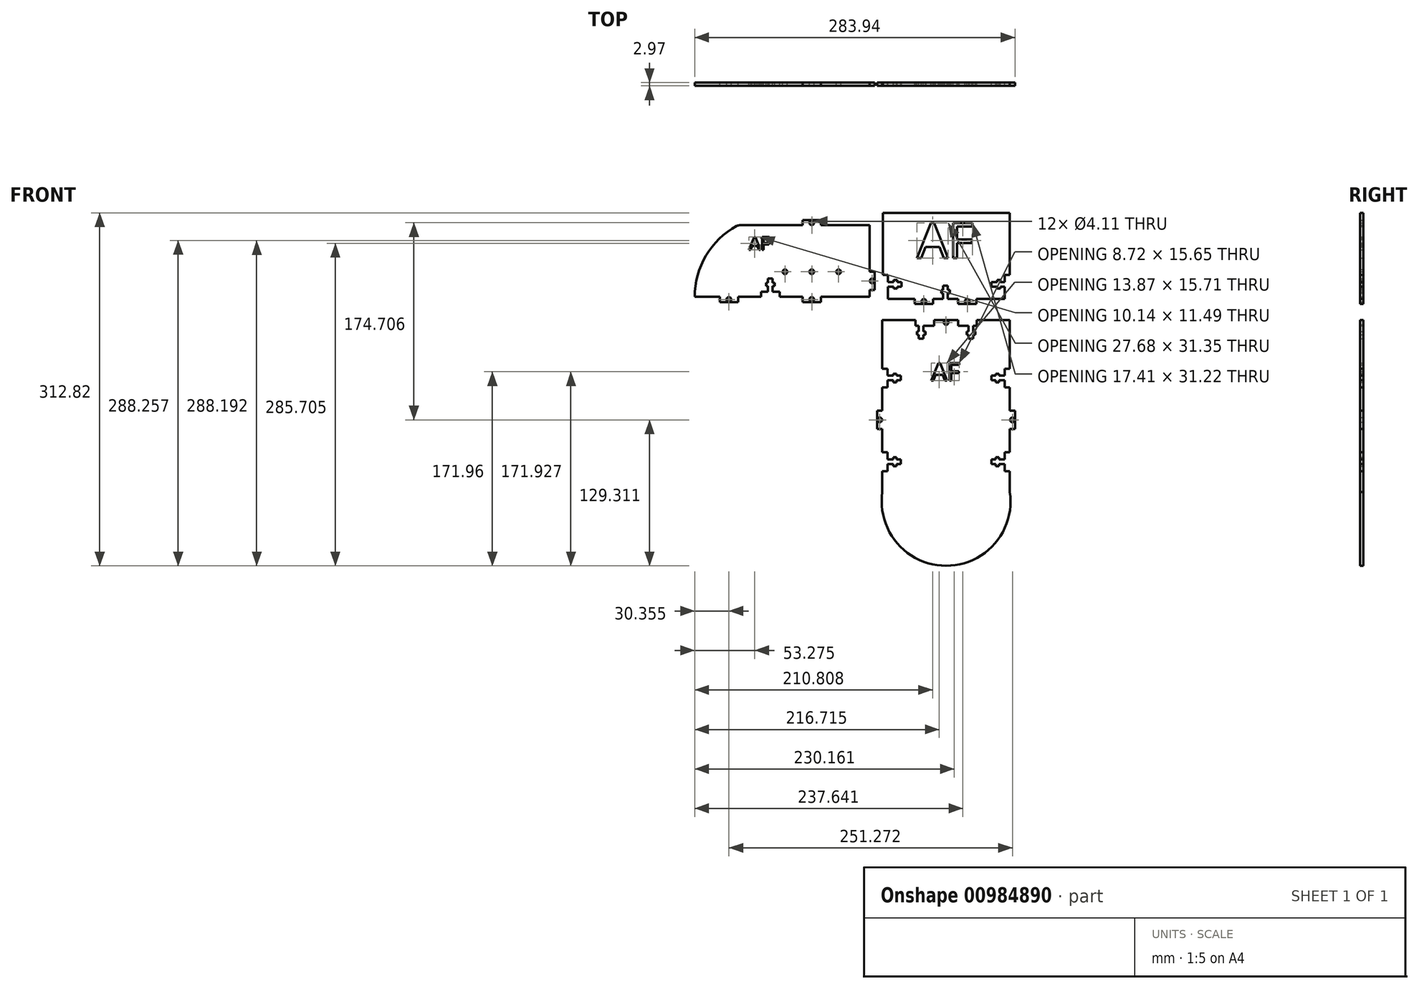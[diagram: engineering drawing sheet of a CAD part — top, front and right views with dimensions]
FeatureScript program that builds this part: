
annotation { "Feature Type Name" : "Feature", "Feature Type Description" : "" }
export const myFeature = defineFeature(function(context is Context, id is Id, definition is map)
    precondition{}
    {
        {
            var Q0;
            Q0=qCreatedBy(makeId("Front.planeOp"),FACE);
            var sketch = newSketch(context, id + "F0", { "sketchPlane" : qUnion([Q0])});
            skCircle(sketch, "E0", {"center": v(-10.51, -12.98) * mm, "radius": 2.06 * mm});
            skLineSegment(sketch, "E1.top", {"start": v(-18.6, -15.29) * mm, "end": v(-2.43, -15.29) * mm});
            skCircle(sketch, "E2", {"center": v(27.94, -12.98) * mm, "radius": 2.06 * mm});
            skLineSegment(sketch, "E3", {"start": v(19.85, -15.29) * mm, "end": v(36.02, -15.29) * mm});
            skLineSegment(sketch, "E4", {"start": v(-38.26, -10.74) * mm, "end": v(-18.6, -10.74) * mm});
            skLineSegment(sketch, "E5", {"start": v(-2.43, -15.29) * mm, "end": v(-2.43, -10.74) * mm});
            skLineSegment(sketch, "E6", {"start": v(-18.6, -15.29) * mm, "end": v(-18.6, -10.74) * mm});
            skLineSegment(sketch, "E7", {"start": v(36.02, -15.29) * mm, "end": v(36.02, -10.74) * mm});
            skLineSegment(sketch, "E8", {"start": v(19.85, -15.29) * mm, "end": v(19.85, -10.74) * mm});
            skLineSegment(sketch, "E9.trimOffspring", {"start": v(-2.43, -10.74) * mm, "end": v(6.65, -10.74) * mm});
            skLineSegment(sketch, "E10.trimOffspring", {"start": v(36.02, -10.74) * mm, "end": v(58.06, -10.74) * mm});
            skLineSegment(sketch, "E11", {"start": v(-38.26, -10.74) * mm, "end": v(-42.22, -10.74) * mm});
            skLineSegment(sketch, "E12", {"start": v(58.06, -10.74) * mm, "end": v(61.06, -10.74) * mm});
            skLineSegment(sketch, "E13", {"start": v(65.6, 14.43) * mm, "end": v(65.6, 10.39) * mm});
            skLineSegment(sketch, "E14", {"start": v(-46.77, 14.3) * mm, "end": v(-46.77, 10.39) * mm});
            skLineSegment(sketch, "E15", {"start": v(-46.77, 10.39) * mm, "end": v(-42.22, 10.39) * mm});
            skLineSegment(sketch, "E16", {"start": v(-42.22, 10.39) * mm, "end": v(-42.22, 4.11) * mm});
            skLineSegment(sketch, "E17", {"start": v(65.6, 10.39) * mm, "end": v(61.06, 10.39) * mm});
            skLineSegment(sketch, "E18", {"start": v(61.06, 10.39) * mm, "end": v(61.06, 4.11) * mm});
            skLineSegment(sketch, "E19", {"start": v(61.06, 0) * mm, "end": v(57.32, 0) * mm});
            skLineSegment(sketch, "E20.trimOffspring", {"start": v(61.06, 0) * mm, "end": v(61.06, -6.27) * mm});
            skLineSegment(sketch, "E21", {"start": v(-42.22, 0) * mm, "end": v(-37.14, 0) * mm});
            skLineSegment(sketch, "E22.trimOffspring", {"start": v(-42.22, 0) * mm, "end": v(-42.22, -6.27) * mm});
            skLineSegment(sketch, "E23", {"start": v(6.65, -10.74) * mm, "end": v(6.65, -5.66) * mm});
            skLineSegment(sketch, "E24.trimOffspring", {"start": v(10.77, -10.74) * mm, "end": v(19.85, -10.74) * mm});
            skLineSegment(sketch, "E25", {"start": v(-46.77, 14.3) * mm, "end": v(-46.77, 65.46) * mm});
            skLineSegment(sketch, "E26", {"start": v(65.6, 14.43) * mm, "end": v(65.6, 65.46) * mm});
            skLineSegment(sketch, "E27", {"start": v(-46.77, 65.46) * mm, "end": v(65.6, 65.46) * mm});
            skLineSegment(sketch, "E28.trimOffspring", {"start": v(-30.47, 4.11) * mm, "end": v(-34.21, 4.11) * mm});
            skLineSegment(sketch, "E29.trimOffspring", {"start": v(49.32, 4.11) * mm, "end": v(54.4, 4.11) * mm});
            skLineSegment(sketch, "E30.trimOffspring", {"start": v(10.77, 1) * mm, "end": v(10.77, -2.74) * mm});
            skLineSegment(sketch, "E31", {"start": v(49.32, 4.11) * mm, "end": v(49.32, 0) * mm});
            skPoint(sketch, "E32.startSnap0", {"position": v(49.32, -3.14) * mm});
            skPoint(sketch, "E33.end.orphan", {"position": v(49.32, 10.39) * mm});
            skPoint(sketch, "E34.end.orphan", {"position": v(43.4, 10.39) * mm});
            skPoint(sketch, "E35.end.orphan", {"position": v(43.4, 4.11) * mm});
            skPoint(sketch, "E36.end.orphan", {"position": v(37.56, 4.11) * mm});
            skPoint(sketch, "E37.trimOffspring.end.orphan", {"position": v(37.56, 0) * mm});
            skPoint(sketch, "E38.end.orphan", {"position": v(43.4, 0) * mm});
            skPoint(sketch, "E39.end.orphan", {"position": v(43.4, -6.27) * mm});
            skPoint(sketch, "E40.orphan", {"position": v(49.32, -6.27) * mm});
            skLineSegment(sketch, "E41", {"start": v(54.4, -1.78) * mm, "end": v(57.32, -1.78) * mm});
            skLineSegment(sketch, "E42", {"start": v(57.32, -1.78) * mm, "end": v(57.32, 0) * mm});
            skLineSegment(sketch, "E43", {"start": v(54.4, 4.11) * mm, "end": v(54.4, 5.9) * mm});
            skLineSegment(sketch, "E44", {"start": v(54.4, 5.9) * mm, "end": v(57.3, 5.9) * mm});
            skLineSegment(sketch, "E45", {"start": v(57.3, 5.9) * mm, "end": v(57.3, 4.11) * mm});
            skLineSegment(sketch, "E46.trimOffspring", {"start": v(57.3, 4.11) * mm, "end": v(61.06, 4.11) * mm});
            skLineSegment(sketch, "E47", {"start": v(54.4, 0) * mm, "end": v(54.4, -1.78) * mm});
            skLineSegment(sketch, "E48.trimOffspring", {"start": v(54.4, 0) * mm, "end": v(49.32, 0) * mm});
            skLineSegment(sketch, "E49", {"start": v(-30.47, 4.11) * mm, "end": v(-30.47, 0) * mm});
            skLineSegment(sketch, "E50", {"start": v(6.65, 1) * mm, "end": v(10.77, 1) * mm});
            skLineSegment(sketch, "E51", {"start": v(61.06, -6.27) * mm, "end": v(61.06, -10.74) * mm});
            skPoint(sketch, "E52.orphan", {"position": v(65.6, -10.74) * mm});
            skPoint(sketch, "E53.start.orphan", {"position": v(65.6, -6.27) * mm});
            skLineSegment(sketch, "E54", {"start": v(-42.22, -6.27) * mm, "end": v(-42.22, -10.74) * mm});
            skPoint(sketch, "E55.orphan", {"position": v(-46.77, -10.74) * mm});
            skLineSegment(sketch, "E56", {"start": v(-37.14, 4.11) * mm, "end": v(-37.14, 5.9) * mm});
            skLineSegment(sketch, "E57", {"start": v(-37.14, 5.9) * mm, "end": v(-34.21, 5.9) * mm});
            skLineSegment(sketch, "E58", {"start": v(-34.21, 5.9) * mm, "end": v(-34.21, 4.11) * mm});
            skLineSegment(sketch, "E59.trimOffspring", {"start": v(-37.14, 4.11) * mm, "end": v(-42.22, 4.11) * mm});
            skLineSegment(sketch, "E60.trimOffspring", {"start": v(-34.21, 0) * mm, "end": v(-30.47, 0) * mm});
            skLineSegment(sketch, "E61", {"start": v(-37.14, 0) * mm, "end": v(-37.14, -1.75) * mm});
            skLineSegment(sketch, "E62", {"start": v(-37.14, -1.75) * mm, "end": v(-34.21, -1.75) * mm});
            skLineSegment(sketch, "E63", {"start": v(-34.21, -1.75) * mm, "end": v(-34.21, 0) * mm});
            skLineSegment(sketch, "E64", {"start": v(4.88, -5.66) * mm, "end": v(6.65, -5.66) * mm});
            skLineSegment(sketch, "E65", {"start": v(4.88, -5.66) * mm, "end": v(4.88, -2.74) * mm});
            skLineSegment(sketch, "E66", {"start": v(4.88, -2.74) * mm, "end": v(6.65, -2.74) * mm});
            skLineSegment(sketch, "E67", {"start": v(10.77, -5.66) * mm, "end": v(12.55, -5.66) * mm});
            skLineSegment(sketch, "E68", {"start": v(12.55, -5.66) * mm, "end": v(12.55, -2.74) * mm});
            skLineSegment(sketch, "E69", {"start": v(12.55, -2.74) * mm, "end": v(10.77, -2.74) * mm});
            skLineSegment(sketch, "E70.trimOffspring", {"start": v(10.77, -5.66) * mm, "end": v(10.77, -10.74) * mm});
            skLineSegment(sketch, "E71.trimOffspring", {"start": v(6.65, -2.74) * mm, "end": v(6.65, 1) * mm});
            skText(sketch, "E72", { "text": "AF", "fontName": "OpenSans-Regular.ttf"});
            const initialGuessF0  = {"E72": [-0.0167, 0.02522, 1, 0, 0.03149]};
            skSetInitialGuess(sketch, initialGuessF0);
            skSolve(sketch);
        }
        {
            var Q0;
            Q0=makeQuery(id+"F0.imprint","IMPRINT",FACE,{"disambiguationData":[TD([[makeQuery(id+"F0.imprint","IMPRINT",EDGE,{"derivedFrom":sQuery(id+"F0.wireOp",EDGE,"E0")}),-1.0]])]});
            extrude(context, id + "F1", {"entities" : qUnion([Q0]), "depth" : 2.97 * mm, "offsetDistance" : 25.4 * mm});
        }
        {
            var Q0;
            Q0=qCreatedBy(makeId("Front.planeOp"),FACE);
            var sketch = newSketch(context, id + "F2", { "sketchPlane" : qUnion([Q0])});
            skLineSegment(sketch, "E73", {"start": v(-36, -9.08) * mm, "end": v(-36, -2.95) * mm});
            skLineSegment(sketch, "E74", {"start": v(-31.45, -2.95) * mm, "end": v(-31.45, 13.2) * mm});
            skLineSegment(sketch, "E75", {"start": v(-31.45, 13.2) * mm, "end": v(-36, 13.2) * mm});
            skLineSegment(sketch, "E76", {"start": v(-31.45, -2.95) * mm, "end": v(-36, -2.95) * mm});
            skCircle(sketch, "E77", {"center": v(-33.76, 5.12) * mm, "radius": 2.06 * mm});
            skLineSegment(sketch, "E78", {"start": v(-36, -9.08) * mm, "end": v(-79.18, -9.08) * mm});
            skLineSegment(sketch, "E79", {"start": v(-79.18, -13.62) * mm, "end": v(-79.18, -9.08) * mm});
            skLineSegment(sketch, "E80", {"start": v(-79.18, -13.62) * mm, "end": v(-95.33, -13.62) * mm});
            skLineSegment(sketch, "E81", {"start": v(-95.33, -13.62) * mm, "end": v(-95.33, -9.08) * mm});
            skCircle(sketch, "E82", {"center": v(-87.25, -11.31) * mm, "radius": 2.06 * mm});
            skPoint(sketch, "E82.centerSnap0", {"position": v(-87.25, -13.62) * mm});
            skLineSegment(sketch, "E83", {"start": v(-115.65, -9.08) * mm, "end": v(-115.65, -4.53) * mm});
            skLineSegment(sketch, "E84", {"start": v(-132.31, -9.08) * mm, "end": v(-132.31, -4.53) * mm});
            skLineSegment(sketch, "E85", {"start": v(-132.31, -4.53) * mm, "end": v(-126.04, -4.53) * mm});
            skLineSegment(sketch, "E86.trimOffspring", {"start": v(-132.31, -9.08) * mm, "end": v(-152.63, -9.08) * mm});
            skLineSegment(sketch, "E87", {"start": v(-126.04, -4.53) * mm, "end": v(-126.04, 0.55) * mm});
            skLineSegment(sketch, "E88", {"start": v(-152.63, -13.62) * mm, "end": v(-152.63, -9.08) * mm});
            skLineSegment(sketch, "E89", {"start": v(-152.63, -13.62) * mm, "end": v(-168.79, -13.62) * mm});
            skLineSegment(sketch, "E90", {"start": v(-168.79, -13.62) * mm, "end": v(-168.79, -9.08) * mm});
            skCircle(sketch, "E91", {"center": v(-160.7, -11.31) * mm, "radius": 2.06 * mm});
            skPoint(sketch, "E91.centerSnap0", {"position": v(-160.7, -13.62) * mm});
            skLineSegment(sketch, "E92", {"start": v(-36, 54.42) * mm, "end": v(-79.18, 54.42) * mm});
            skPoint(sketch, "E93.centerSnap0", {"position": v(-124.36, 18.96) * mm});
            skLineSegment(sketch, "E94.trimOffspring", {"start": v(-95.33, -9.08) * mm, "end": v(-115.65, -9.08) * mm});
            skLineSegment(sketch, "E95.trimOffspring", {"start": v(-36, 13.2) * mm, "end": v(-36, 54.42) * mm});
            skLineSegment(sketch, "E96", {"start": v(-191.06, -9.08) * mm, "end": v(-168.79, -9.08) * mm});
            skPoint(sketch, "E97.start.orphan", {"position": v(-126.81, 13.13) * mm});
            skLineSegment(sketch, "E98", {"start": v(-126.04, 7.22) * mm, "end": v(-121.92, 7.22) * mm});
            skLineSegment(sketch, "E99", {"start": v(-121.92, -4.53) * mm, "end": v(-115.65, -4.53) * mm});
            skLineSegment(sketch, "E100", {"start": v(-121.92, 7.22) * mm, "end": v(-121.92, 3.47) * mm});
            skLineSegment(sketch, "E101", {"start": v(-121.92, 0.55) * mm, "end": v(-120.15, 0.55) * mm});
            skPoint(sketch, "E101.startSnap0", {"position": v(-121.92, 1.34) * mm});
            skLineSegment(sketch, "E102", {"start": v(-120.15, 0.55) * mm, "end": v(-120.15, 3.47) * mm});
            skLineSegment(sketch, "E103", {"start": v(-120.15, 3.47) * mm, "end": v(-121.92, 3.47) * mm});
            skLineSegment(sketch, "E104", {"start": v(-126.04, 3.47) * mm, "end": v(-127.82, 3.47) * mm});
            skLineSegment(sketch, "E105", {"start": v(-127.82, 3.47) * mm, "end": v(-127.82, 0.55) * mm});
            skLineSegment(sketch, "E106", {"start": v(-127.82, 0.55) * mm, "end": v(-126.04, 0.55) * mm});
            skLineSegment(sketch, "E107.trimOffspring", {"start": v(-126.04, 3.47) * mm, "end": v(-126.04, 7.22) * mm});
            skLineSegment(sketch, "E108.trimOffspring", {"start": v(-121.92, 0.55) * mm, "end": v(-121.92, -4.53) * mm});
            skLineSegment(sketch, "E109.trimOffspring", {"start": v(-168.79, 54.42) * mm, "end": v(-191.06, 54.42) * mm});
            skPoint(sketch, "E110", {"position": v(-87.25, 13.2) * mm});
            skCircle(sketch, "E111", {"center": v(-87.25, 13.2) * mm, "radius": 2.06 * mm});
            skCircle(sketch, "E112", {"center": v(-110.98, 13.2) * mm, "radius": 2.06 * mm});
            skCircle(sketch, "E113", {"center": v(-63.53, 13.2) * mm, "radius": 2.06 * mm});
            skLineSegment(sketch, "E114", {"start": v(-191.06, 54.42) * mm, "end": v(-191.06, -9.08) * mm});
            skLineSegment(sketch, "E115", {"start": v(-168.79, 54.42) * mm, "end": v(-152.63, 54.42) * mm});
            skLineSegment(sketch, "E116", {"start": v(-95.33, 54.42) * mm, "end": v(-95.33, 58.97) * mm});
            skLineSegment(sketch, "E117", {"start": v(-95.33, 58.97) * mm, "end": v(-79.18, 58.97) * mm});
            skLineSegment(sketch, "E118", {"start": v(-79.18, 58.97) * mm, "end": v(-79.18, 54.42) * mm});
            skCircle(sketch, "E119", {"center": v(-87.25, 56.66) * mm, "radius": 2.06 * mm});
            skPoint(sketch, "E119.centerSnap0", {"position": v(-87.25, 58.97) * mm});
            skLineSegment(sketch, "E120.trimOffspring", {"start": v(-95.33, 54.42) * mm, "end": v(-152.63, 54.42) * mm});
            skArc(sketch, "E121", {"start": v(-152.63, 54.42) * mm, "mid": v(-180.7, 28.03) * mm, "end": v(-191.06, -9.08) * mm});
            skText(sketch, "E122", { "text": "AF", "fontName": "OpenSans-Regular.ttf"});
            const initialGuessF2  = {"E122": [-0.14286, 0.0326, 1, 0, 0.01154]};
            skSetInitialGuess(sketch, initialGuessF2);
            skSolve(sketch);
        }
        {
            var Q0;
            {var subQ1=sQuery(id+"F2.wireOp",EDGE,"OVJFDN25-UqmM-4DHd-mgfS-xPrGIr8piSGO");Q0=makeQuery(id+"F2.imprint","IMPRINT",FACE,{"disambiguationData":[TD([[makeQuery(id+"F2.imprint","IMPRINT",EDGE,{"derivedFrom":subQ1}),-1.0]])]});}
            var Q1;
            {var subQ2=sQuery(id+"F2.wireOp",EDGE,"OVJFDN25-UqmM-4DHd-mgfS-xPrGIr8piSGO");Q1=makeQuery(id+"F2.imprint","IMPRINT",FACE,{"disambiguationData":[TD([[makeQuery(id+"F2.imprint","IMPRINT",EDGE,{"derivedFrom":subQ2}),1.0]])]});}
            var Q2;
            {var subQ1=sQuery(id+"F2.wireOp",EDGE,"E79");Q2=makeQuery(id+"F2.imprint","IMPRINT",FACE,{"disambiguationData":[TD([[makeQuery(id+"F2.imprint","IMPRINT",EDGE,{"derivedFrom":subQ1}),1.0]])]});}
            extrude(context, id + "F3", {"entities" : qUnion([Q0, Q1, Q2]), "depth" : 2.97 * mm, "offsetDistance" : 25.4 * mm});
        }
        {
            var Q0;
            Q0=qCreatedBy(makeId("Front.planeOp"),FACE);
            var sketch = newSketch(context, id + "F4", { "sketchPlane" : qUnion([Q0])});
            skLineSegment(sketch, "E123", {"start": v(-47.3, -38.57) * mm, "end": v(-17.97, -38.57) * mm});
            skLineSegment(sketch, "E124", {"start": v(65.7, -38.57) * mm, "end": v(65.7, -81.75) * mm});
            skLineSegment(sketch, "E125", {"start": v(-47.3, -38.57) * mm, "end": v(-47.3, -81.75) * mm});
            skLineSegment(sketch, "E126", {"start": v(-47.3, -190.97) * mm, "end": v(65.7, -190.97) * mm});
            skLineSegment(sketch, "E127", {"start": v(65.7, -38.57) * mm, "end": v(35.47, -38.57) * mm});
            skLineSegment(sketch, "E128", {"start": v(-1.3, -43.64) * mm, "end": v(-1.3, -38.57) * mm});
            skLineSegment(sketch, "E129", {"start": v(-1.3, -43.64) * mm, "end": v(-10.82, -43.64) * mm});
            skLineSegment(sketch, "E130.trimOffspring", {"start": v(-1.3, -38.57) * mm, "end": v(19.7, -38.57) * mm});
            skLineSegment(sketch, "E131.trimOffspring", {"start": v(35.47, -38.57) * mm, "end": v(65.7, -38.57) * mm});
            skCircle(sketch, "E132", {"center": v(9.2, -40.88) * mm, "radius": 2.06 * mm});
            skLineSegment(sketch, "E133", {"start": v(-17.97, -43.64) * mm, "end": v(-17.97, -38.57) * mm});
            skLineSegment(sketch, "E134", {"start": v(35.47, -38.57) * mm, "end": v(36.36, -38.57) * mm});
            skLineSegment(sketch, "E135", {"start": v(-17.97, -43.64) * mm, "end": v(-14.94, -43.64) * mm});
            skLineSegment(sketch, "E136", {"start": v(-14.94, -43.64) * mm, "end": v(-14.94, -48.72) * mm});
            skPoint(sketch, "E137.end.orphan", {"position": v(-8.78, -55.39) * mm});
            skLineSegment(sketch, "E138", {"start": v(-10.82, -43.64) * mm, "end": v(-10.82, -48.72) * mm});
            skLineSegment(sketch, "E139", {"start": v(-47.3, -81.75) * mm, "end": v(-42.74, -81.75) * mm});
            skLineSegment(sketch, "E140", {"start": v(-42.74, -98.41) * mm, "end": v(-47.3, -98.41) * mm});
            skLineSegment(sketch, "E141.trimOffspring", {"start": v(-47.3, -98.41) * mm, "end": v(-47.3, -119.12) * mm});
            skLineSegment(sketch, "E142", {"start": v(-42.74, -81.75) * mm, "end": v(-42.74, -88.02) * mm});
            skLineSegment(sketch, "E143", {"start": v(-42.74, -98.41) * mm, "end": v(-42.74, -92.14) * mm});
            skPoint(sketch, "E144.start.orphan", {"position": v(-42.74, -38.57) * mm});
            skLineSegment(sketch, "E145", {"start": v(-47.3, -119.12) * mm, "end": v(-51.88, -119.12) * mm});
            skLineSegment(sketch, "E146", {"start": v(-51.88, -119.12) * mm, "end": v(-51.88, -135.27) * mm});
            skLineSegment(sketch, "E147", {"start": v(-51.88, -135.27) * mm, "end": v(-47.3, -135.27) * mm});
            skPoint(sketch, "E148.start.orphan", {"position": v(-42.74, -118.73) * mm});
            skLineSegment(sketch, "E149.trimOffspring", {"start": v(-47.3, -135.27) * mm, "end": v(-47.3, -155.97) * mm});
            skCircle(sketch, "E150", {"center": v(-49.57, -127.2) * mm, "radius": 2.06 * mm});
            skLineSegment(sketch, "E151", {"start": v(-47.3, -155.97) * mm, "end": v(-42.74, -155.97) * mm});
            skLineSegment(sketch, "E152", {"start": v(-42.74, -172.63) * mm, "end": v(-47.3, -172.63) * mm});
            skLineSegment(sketch, "E153.trimOffspring", {"start": v(-47.3, -172.63) * mm, "end": v(-47.3, -190.97) * mm});
            skLineSegment(sketch, "E154", {"start": v(-42.74, -172.63) * mm, "end": v(-42.74, -166.36) * mm});
            skLineSegment(sketch, "E155", {"start": v(-42.74, -155.97) * mm, "end": v(-42.74, -162.24) * mm});
            skLineSegment(sketch, "E156", {"start": v(-42.74, -162.24) * mm, "end": v(-37.66, -162.24) * mm});
            skLineSegment(sketch, "E157", {"start": v(-42.74, -166.36) * mm, "end": v(-37.66, -166.36) * mm});
            skLineSegment(sketch, "E158", {"start": v(-42.74, -88.02) * mm, "end": v(-37.66, -88.02) * mm});
            skLineSegment(sketch, "E159", {"start": v(-42.74, -92.14) * mm, "end": v(-37.66, -92.14) * mm});
            skLineSegment(sketch, "E160", {"start": v(9.2, -40.88) * mm, "end": v(9.2, -38.57) * mm});
            skLineSegment(sketch, "E161", {"start": v(9.2, -40.88) * mm, "end": v(9.2, -190.97) * mm, "construction": true});
            skLineSegment(sketch, "E162.MirrorCS", {"start": v(65.7, -135.27) * mm, "end": v(65.7, -155.97) * mm});
            skLineSegment(sketch, "E163.MirrorCS", {"start": v(65.7, -172.63) * mm, "end": v(65.7, -190.97) * mm});
            skLineSegment(sketch, "E164.MirrorCS", {"start": v(65.7, -98.41) * mm, "end": v(65.7, -119.12) * mm});
            skPoint(sketch, "E165.MirrorP", {"position": v(61.12, -118.73) * mm});
            skLineSegment(sketch, "E166", {"start": v(-14.94, -55.37) * mm, "end": v(-10.82, -55.37) * mm});
            skLineSegment(sketch, "E167", {"start": v(-31, -92.14) * mm, "end": v(-31, -88.02) * mm});
            skLineSegment(sketch, "E168", {"start": v(-31, -162.24) * mm, "end": v(-31, -166.36) * mm});
            skPoint(sketch, "E169.start.orphan", {"position": v(-31, -155.6) * mm});
            skPoint(sketch, "E170.start.orphan", {"position": v(-31, -173.01) * mm});
            skPoint(sketch, "E171.end.orphan", {"position": v(-31, -98.03) * mm});
            skPoint(sketch, "E172.start.orphan", {"position": v(-25.08, -98.03) * mm});
            skPoint(sketch, "E173.start.orphan", {"position": v(-25.08, -92.14) * mm});
            skPoint(sketch, "E174.end.orphan", {"position": v(-19.24, -88.02) * mm});
            skPoint(sketch, "E174.start.orphan", {"position": v(-19.24, -91.37) * mm});
            skPoint(sketch, "E175.start.orphan", {"position": v(-31, -81.37) * mm});
            skPoint(sketch, "E176.end.orphan", {"position": v(-25.08, -88.02) * mm});
            skPoint(sketch, "E176.start.orphan", {"position": v(-25.08, -81.37) * mm});
            skPoint(sketch, "E177.start.orphan", {"position": v(-10.82, -67.1) * mm});
            skPoint(sketch, "E178.end.orphan", {"position": v(-14.94, -67.1) * mm});
            skPoint(sketch, "E179.end.orphan", {"position": v(-10.82, -61.3) * mm});
            skPoint(sketch, "E180.end.orphan", {"position": v(-1.3, -61.3) * mm});
            skPoint(sketch, "E181.end.orphan", {"position": v(-1.3, -55.37) * mm});
            skPoint(sketch, "E182.end.orphan", {"position": v(-14.94, -61.33) * mm});
            skPoint(sketch, "E183.end.orphan", {"position": v(-17.97, -61.3) * mm});
            skPoint(sketch, "E184.end.orphan", {"position": v(-17.97, -55.37) * mm});
            skLineSegment(sketch, "E185", {"start": v(-37.66, -93.91) * mm, "end": v(-37.66, -92.14) * mm});
            skLineSegment(sketch, "E186", {"start": v(-37.66, -93.91) * mm, "end": v(-34.74, -93.91) * mm});
            skLineSegment(sketch, "E187", {"start": v(-34.74, -93.91) * mm, "end": v(-34.74, -92.14) * mm});
            skLineSegment(sketch, "E188", {"start": v(-37.66, -88.02) * mm, "end": v(-37.66, -86.24) * mm});
            skLineSegment(sketch, "E189", {"start": v(-37.66, -86.24) * mm, "end": v(-34.74, -86.24) * mm});
            skLineSegment(sketch, "E190", {"start": v(-34.74, -86.24) * mm, "end": v(-34.75, -88.02) * mm});
            skLineSegment(sketch, "E191.trimOffspring", {"start": v(-34.75, -88.02) * mm, "end": v(-31, -88.02) * mm});
            skLineSegment(sketch, "E192.trimOffspring", {"start": v(-34.74, -92.14) * mm, "end": v(-31, -92.14) * mm});
            skLineSegment(sketch, "E193", {"start": v(-37.66, -162.24) * mm, "end": v(-37.66, -160.47) * mm});
            skLineSegment(sketch, "E194", {"start": v(-37.66, -166.36) * mm, "end": v(-37.66, -168.13) * mm});
            skLineSegment(sketch, "E195", {"start": v(-37.66, -168.13) * mm, "end": v(-34.74, -168.13) * mm});
            skLineSegment(sketch, "E196", {"start": v(-34.74, -168.13) * mm, "end": v(-34.74, -166.36) * mm});
            skLineSegment(sketch, "E197", {"start": v(-37.66, -160.47) * mm, "end": v(-34.74, -160.47) * mm});
            skLineSegment(sketch, "E198", {"start": v(-34.74, -160.47) * mm, "end": v(-34.74, -162.24) * mm});
            skLineSegment(sketch, "E199.trimOffspring", {"start": v(-34.74, -162.24) * mm, "end": v(-31, -162.24) * mm});
            skLineSegment(sketch, "E200.trimOffspring", {"start": v(-34.74, -166.36) * mm, "end": v(-31, -166.36) * mm});
            skLineSegment(sketch, "E201", {"start": v(-16.71, -48.72) * mm, "end": v(-14.94, -48.72) * mm});
            skLineSegment(sketch, "E202", {"start": v(-16.71, -48.72) * mm, "end": v(-16.71, -51.64) * mm});
            skLineSegment(sketch, "E203", {"start": v(-16.71, -51.64) * mm, "end": v(-14.94, -51.64) * mm});
            skLineSegment(sketch, "E204", {"start": v(-10.82, -48.72) * mm, "end": v(-9.04, -48.72) * mm});
            skLineSegment(sketch, "E205", {"start": v(-9.04, -48.72) * mm, "end": v(-9.04, -51.64) * mm});
            skLineSegment(sketch, "E206", {"start": v(-9.04, -51.64) * mm, "end": v(-10.82, -51.64) * mm});
            skLineSegment(sketch, "E207.trimOffspring", {"start": v(-10.82, -51.64) * mm, "end": v(-10.82, -55.37) * mm});
            skLineSegment(sketch, "E208.trimOffspring", {"start": v(-14.94, -51.64) * mm, "end": v(-14.94, -55.37) * mm});
            skLineSegment(sketch, "E209", {"start": v(65.8, -135.27) * mm, "end": v(65.8, -135.44) * mm});
            skLineSegment(sketch, "E210.MirrorCS", {"start": v(53.13, -160.47) * mm, "end": v(53.13, -162.24) * mm});
            skLineSegment(sketch, "E211.MirrorCS", {"start": v(56.05, -88.02) * mm, "end": v(56.05, -86.24) * mm});
            skLineSegment(sketch, "E212.MirrorCS", {"start": v(33.32, -51.64) * mm, "end": v(33.32, -55.37) * mm});
            skLineSegment(sketch, "E213.MirrorCS", {"start": v(56.05, -86.24) * mm, "end": v(53.13, -86.24) * mm});
            skLineSegment(sketch, "E214.MirrorCS", {"start": v(53.13, -86.24) * mm, "end": v(53.14, -88.02) * mm});
            skLineSegment(sketch, "E215.MirrorCS", {"start": v(33.32, -43.64) * mm, "end": v(33.32, -48.72) * mm});
            skLineSegment(sketch, "E216.MirrorCS", {"start": v(53.13, -93.91) * mm, "end": v(53.13, -92.14) * mm});
            skLineSegment(sketch, "E217.MirrorCS", {"start": v(56.05, -93.91) * mm, "end": v(56.05, -92.14) * mm});
            skLineSegment(sketch, "E218.MirrorCS", {"start": v(61.12, -166.36) * mm, "end": v(56.05, -166.36) * mm});
            skLineSegment(sketch, "E219.MirrorCS", {"start": v(56.05, -93.91) * mm, "end": v(53.13, -93.91) * mm});
            skLineSegment(sketch, "E220.MirrorCS", {"start": v(53.13, -92.14) * mm, "end": v(49.39, -92.14) * mm});
            skLineSegment(sketch, "E221.MirrorCS", {"start": v(56.05, -160.47) * mm, "end": v(53.13, -160.47) * mm});
            skLineSegment(sketch, "E222.MirrorCS", {"start": v(35.1, -51.64) * mm, "end": v(33.32, -51.64) * mm});
            skLineSegment(sketch, "E223.MirrorCS", {"start": v(70.27, -135.27) * mm, "end": v(65.7, -135.27) * mm});
            skLineSegment(sketch, "E224.MirrorCS", {"start": v(53.13, -162.24) * mm, "end": v(49.39, -162.24) * mm});
            skLineSegment(sketch, "E225.MirrorCS", {"start": v(56.05, -162.24) * mm, "end": v(56.05, -160.47) * mm});
            skLineSegment(sketch, "E226.MirrorCS", {"start": v(49.39, -162.24) * mm, "end": v(49.39, -166.36) * mm});
            skLineSegment(sketch, "E227.MirrorCS", {"start": v(29.2, -48.72) * mm, "end": v(27.43, -48.72) * mm});
            skLineSegment(sketch, "E228.MirrorCS", {"start": v(53.14, -88.02) * mm, "end": v(49.39, -88.02) * mm});
            skLineSegment(sketch, "E229.MirrorCS", {"start": v(29.2, -43.64) * mm, "end": v(29.2, -48.72) * mm});
            skLineSegment(sketch, "E230.MirrorCS", {"start": v(33.32, -55.37) * mm, "end": v(29.2, -55.37) * mm});
            skLineSegment(sketch, "E231.MirrorCS", {"start": v(49.39, -92.14) * mm, "end": v(49.39, -88.02) * mm});
            skLineSegment(sketch, "E232.MirrorCS", {"start": v(61.12, -88.02) * mm, "end": v(56.05, -88.02) * mm});
            skLineSegment(sketch, "E233.MirrorCS", {"start": v(35.1, -48.72) * mm, "end": v(33.32, -48.72) * mm});
            skLineSegment(sketch, "E234.MirrorCS", {"start": v(56.05, -168.13) * mm, "end": v(53.13, -168.13) * mm});
            skLineSegment(sketch, "E235.MirrorCS", {"start": v(56.05, -166.36) * mm, "end": v(56.05, -168.13) * mm});
            skLineSegment(sketch, "E236.MirrorCS", {"start": v(53.13, -168.13) * mm, "end": v(53.13, -166.36) * mm});
            skLineSegment(sketch, "E237.MirrorCS", {"start": v(27.43, -48.72) * mm, "end": v(27.43, -51.64) * mm});
            skLineSegment(sketch, "E238.MirrorCS", {"start": v(35.1, -48.72) * mm, "end": v(35.1, -51.64) * mm});
            skLineSegment(sketch, "E239.MirrorCS", {"start": v(53.13, -166.36) * mm, "end": v(49.39, -166.36) * mm});
            skLineSegment(sketch, "E240.MirrorCS", {"start": v(27.43, -51.64) * mm, "end": v(29.2, -51.64) * mm});
            skLineSegment(sketch, "E241.MirrorCS", {"start": v(61.12, -92.14) * mm, "end": v(56.05, -92.14) * mm});
            skLineSegment(sketch, "E242.MirrorCS", {"start": v(65.7, -119.12) * mm, "end": v(70.27, -119.12) * mm});
            skLineSegment(sketch, "E243.MirrorCS", {"start": v(61.12, -172.63) * mm, "end": v(61.12, -166.36) * mm});
            skLineSegment(sketch, "E244.MirrorCS", {"start": v(61.12, -162.24) * mm, "end": v(56.05, -162.24) * mm});
            skLineSegment(sketch, "E245.MirrorCS", {"start": v(19.7, -43.64) * mm, "end": v(19.7, -38.57) * mm});
            skLineSegment(sketch, "E246.MirrorCS", {"start": v(61.12, -81.75) * mm, "end": v(61.12, -88.02) * mm});
            skLineSegment(sketch, "E247.MirrorCS", {"start": v(19.7, -43.64) * mm, "end": v(29.2, -43.64) * mm});
            skLineSegment(sketch, "E248.MirrorCS", {"start": v(29.2, -51.64) * mm, "end": v(29.2, -55.37) * mm});
            skLineSegment(sketch, "E249.MirrorCS", {"start": v(61.12, -98.41) * mm, "end": v(61.12, -92.14) * mm});
            skLineSegment(sketch, "E250.MirrorCS", {"start": v(61.12, -98.41) * mm, "end": v(65.7, -98.41) * mm});
            skLineSegment(sketch, "E251.MirrorCS", {"start": v(61.12, -155.97) * mm, "end": v(61.12, -162.24) * mm});
            skLineSegment(sketch, "E252.MirrorCS", {"start": v(36.36, -43.64) * mm, "end": v(36.36, -38.57) * mm});
            skLineSegment(sketch, "E253.MirrorCS", {"start": v(36.36, -43.64) * mm, "end": v(33.32, -43.64) * mm});
            skLineSegment(sketch, "E254.MirrorCS", {"start": v(65.7, -155.97) * mm, "end": v(61.12, -155.97) * mm});
            skLineSegment(sketch, "E255.MirrorCS", {"start": v(65.7, -81.75) * mm, "end": v(61.12, -81.75) * mm});
            skLineSegment(sketch, "E256.MirrorCS", {"start": v(61.12, -172.63) * mm, "end": v(65.7, -172.63) * mm});
            skPoint(sketch, "E257.MirrorP", {"position": v(49.39, -155.6) * mm});
            skCircle(sketch, "E258.MirrorC", {"center": v(67.96, -127.2) * mm, "radius": 2.06 * mm});
            skPoint(sketch, "E259.MirrorP", {"position": v(43.47, -88.02) * mm});
            skLineSegment(sketch, "E260.MirrorCS", {"start": v(19.7, -38.57) * mm, "end": v(-1.3, -38.57) * mm});
            skPoint(sketch, "E261.MirrorP", {"position": v(29.2, -61.3) * mm});
            skPoint(sketch, "E262.MirrorP", {"position": v(33.32, -61.33) * mm});
            skPoint(sketch, "E263.MirrorP", {"position": v(43.47, -81.37) * mm});
            skPoint(sketch, "E264.MirrorP", {"position": v(27.17, -55.39) * mm});
            skPoint(sketch, "E265.MirrorP", {"position": v(49.39, -81.37) * mm});
            skPoint(sketch, "E266.MirrorP", {"position": v(36.36, -55.37) * mm});
            skPoint(sketch, "E267.MirrorP", {"position": v(61.12, -38.57) * mm});
            skPoint(sketch, "E268.MirrorP", {"position": v(36.36, -61.3) * mm});
            skPoint(sketch, "E269.MirrorP", {"position": v(19.7, -55.37) * mm});
            skPoint(sketch, "E270.MirrorP", {"position": v(37.63, -88.02) * mm});
            skPoint(sketch, "E271.MirrorP", {"position": v(43.47, -92.14) * mm});
            skLineSegment(sketch, "E272.MirrorCS", {"start": v(65.7, -38.57) * mm, "end": v(36.36, -38.57) * mm});
            skPoint(sketch, "E273.MirrorP", {"position": v(37.63, -91.37) * mm});
            skPoint(sketch, "E274.MirrorP", {"position": v(19.7, -61.3) * mm});
            skPoint(sketch, "E275.MirrorP", {"position": v(49.39, -173.01) * mm});
            skPoint(sketch, "E276.MirrorP", {"position": v(49.39, -98.03) * mm});
            skPoint(sketch, "E277.MirrorP", {"position": v(43.47, -98.03) * mm});
            skPoint(sketch, "E278.MirrorP", {"position": v(33.32, -67.1) * mm});
            skPoint(sketch, "E279.MirrorP", {"position": v(29.2, -67.1) * mm});
            skLineSegment(sketch, "E280", {"start": v(70.27, -135.27) * mm, "end": v(70.27, -119.12) * mm});
            skArc(sketch, "E281", {"start": v(-47.3, -190.97) * mm, "mid": v(9.2, -256.5) * mm, "end": v(65.7, -190.97) * mm});
            skText(sketch, "E282", { "text": "AF", "fontName": "OpenSans-Regular.ttf"});
            const initialGuessF4  = {"E282": [-0.00389, -0.0924, 1, 0, 0.01578]};
            skSetInitialGuess(sketch, initialGuessF4);
            skSolve(sketch);
        }
        {
            var Q0;
            Q0=makeQuery(id+"F4.imprint","IMPRINT",FACE,{"disambiguationData":[TD([[makeQuery(id+"F4.imprint","IMPRINT",EDGE,{"derivedFrom":sQuery(id+"F4.wireOp",EDGE,"E123")}),-1.0]])]});
            var Q1;
            Q1=makeQuery(id+"F4.imprint","IMPRINT",FACE,{"disambiguationData":[TD([[makeQuery(id+"F4.imprint","IMPRINT",EDGE,{"derivedFrom":sQuery(id+"F4.wireOp",EDGE,"E126")}),-1.0]])]});
            extrude(context, id + "F5", {"entities" : qUnion([Q0, Q1]), "depth" : 2.97 * mm, "offsetDistance" : 25.4 * mm});
        }
        {
            var Q0;
            Q0=makeQuery(id+"F3.opExtrude","SWEPT_BODY",BODY,{"disambiguationData":[OSD([sQuery(id+"F2.wireOp",EDGE,"E73"),sQuery(id+"F2.wireOp",EDGE,"E74"),sQuery(id+"F2.wireOp",EDGE,"E75"),sQuery(id+"F2.wireOp",EDGE,"E76"),sQuery(id+"F2.wireOp",EDGE,"E77"),sQuery(id+"F2.wireOp",EDGE,"E78"),sQuery(id+"F2.wireOp",EDGE,"E79"),sQuery(id+"F2.wireOp",EDGE,"E80"),sQuery(id+"F2.wireOp",EDGE,"E81"),sQuery(id+"F2.wireOp",EDGE,"E82"),sQuery(id+"F2.wireOp",EDGE,"E83"),sQuery(id+"F2.wireOp",EDGE,"E84"),sQuery(id+"F2.wireOp",EDGE,"smFho10Q-fqs9-7RC2-xNXY-59qUfedKx50k"),sQuery(id+"F2.wireOp",EDGE,"E85"),sQuery(id+"F2.wireOp",EDGE,"E86.trimOffspring"),sQuery(id+"F2.wireOp",EDGE,"E87"),sQuery(id+"F2.wireOp",EDGE,"ADrRUh6O-BrmG-nYIV-0qPf-Y4BKHcjhDC0A"),sQuery(id+"F2.wireOp",EDGE,"3TV9EzE3-sWAf-CArM-Ep5Z-BIaoFF90LYxw"),sQuery(id+"F2.wireOp",EDGE,"a68d64ff-956a-435a-b33e-cca1a7969c3b.trimOffspring"),sQuery(id+"F2.wireOp",EDGE,"5fb2db7f-7043-40fa-93e5-e43134f58009.trimOffspring"),sQuery(id+"F2.wireOp",EDGE,"E88"),sQuery(id+"F2.wireOp",EDGE,"E89"),sQuery(id+"F2.wireOp",EDGE,"E90"),sQuery(id+"F2.wireOp",EDGE,"E91"),sQuery(id+"F2.wireOp",EDGE,"E92"),sQuery(id+"F2.wireOp",EDGE,"Pv8xFsH5-YH5J-F9ey-8Fvg-MMiklTOo1uKY"),sQuery(id+"F2.wireOp",EDGE,"E93"),sQuery(id+"F2.wireOp",EDGE,"E94.trimOffspring"),sQuery(id+"F2.wireOp",EDGE,"E95.trimOffspring"),sQuery(id+"F2.wireOp",EDGE,"E96"),sQuery(id+"F2.wireOp",EDGE,"mWaTCWFI-yoWM-3zpX-jkwn-Rgp68r4fxPfJ"),sQuery(id+"F2.wireOp",EDGE,"91H7TU5L-Fhsu-F0zj-jWK8-o2j0VNuX0pwp"),sQuery(id+"F2.wireOp",EDGE,"qoczEJfj-F8Mu-Nipv-6qPa-pGaxWbRDdk7T"),sQuery(id+"F2.wireOp",EDGE,"wubdM6Ff-gfYk-hoTW-XXbH-Zjq5QOPTjgNT"),sQuery(id+"F2.wireOp",EDGE,"HgigmK6g-IEM9-Paxe-Iuo1-wTw0BSureikm"),sQuery(id+"F2.wireOp",EDGE,"6HSvZUGX-GTlK-ZPIf-wiT4-QNAPdHBzlkyh")])]});
            transform(context, id + "F6", {"entities" : qUnion([Q0]), "transformType" : TransformType.TRANSLATION_3D, "dx" : -22.6 * mm, "dy" : 0 * mm, "dz" : 0 * mm, "makeCopy" : false});
        }
        {
            var Q0;
            Q0=makeQuery(id+"F5.opExtrude","SWEPT_BODY",BODY,{"disambiguationData":[OSD([sQuery(id+"F4.wireOp",EDGE,"E123"),sQuery(id+"F4.wireOp",EDGE,"E125"),sQuery(id+"F4.wireOp",EDGE,"E126"),sQuery(id+"F4.wireOp",EDGE,"iohXHTiQ-WZw0-uzqA-dxWK-AKoeT3LojtUM"),sQuery(id+"F4.wireOp",EDGE,"E128"),sQuery(id+"F4.wireOp",EDGE,"E129"),sQuery(id+"F4.wireOp",EDGE,"E130.trimOffspring"),sQuery(id+"F4.wireOp",EDGE,"E131.trimOffspring"),sQuery(id+"F4.wireOp",EDGE,"E132"),sQuery(id+"F4.wireOp",EDGE,"E133"),sQuery(id+"F4.wireOp",EDGE,"fBH0bQyB-7pDb-zp6R-fFLW-huZ92iLANuKE"),sQuery(id+"F4.wireOp",EDGE,"AZO88fip-mGbl-6Dei-PWM3-G2eas2MXL09o"),sQuery(id+"F4.wireOp",EDGE,"E135"),sQuery(id+"F4.wireOp",EDGE,"433b67b9-89b6-4bd4-9f6b-d9995bbf40bb.trimOffspring"),sQuery(id+"F4.wireOp",EDGE,"djrUTvu5-jOnd-LCKp-OXDw-zwsYnCnUUO5E"),sQuery(id+"F4.wireOp",EDGE,"E136"),sQuery(id+"F4.wireOp",EDGE,"E138"),sQuery(id+"F4.wireOp",EDGE,"E184"),sQuery(id+"F4.wireOp",EDGE,"E181"),sQuery(id+"F4.wireOp",EDGE,"E180"),sQuery(id+"F4.wireOp",EDGE,"E183"),sQuery(id+"F4.wireOp",EDGE,"E182"),sQuery(id+"F4.wireOp",EDGE,"E178"),sQuery(id+"F4.wireOp",EDGE,"E179"),sQuery(id+"F4.wireOp",EDGE,"Iia4y8p5-lMCh-cjUo-4Gru-s2HIaUgALJqL"),sQuery(id+"F4.wireOp",EDGE,"dkRDQeNF-bp09-174G-H3ED-4MkwwZmdMrWS"),sQuery(id+"F4.wireOp",EDGE,"IA7QH3u4-Lbta-FUUF-51SA-xqP7VuBKAvmc"),sQuery(id+"F4.wireOp",EDGE,"VlRwcdI5-8AQM-u4kQ-HBDJ-s0uAhNUMzu6l"),sQuery(id+"F4.wireOp",EDGE,"ICQ3ALdX-dZFh-yGKg-883H-VfHNaUW2OBmi"),sQuery(id+"F4.wireOp",EDGE,"09z2Ze5b-oeJ5-MJT1-rL1R-CWUheOGahaKp"),sQuery(id+"F4.wireOp",EDGE,"kIqyvfzb-Tb18-RJTh-MImL-BTeGV0cvtQuR"),sQuery(id+"F4.wireOp",EDGE,"YpEDKD9l-hypC-jMpX-Njah-JU3KhnVQk5uF"),sQuery(id+"F4.wireOp",EDGE,"zmrpWeGd-UjRu-5kt0-ckeH-GbkOG4DqARqv"),sQuery(id+"F4.wireOp",EDGE,"wBeqmctE-u76Y-yKJe-hdrd-yoPC8vgtup2Y"),sQuery(id+"F4.wireOp",EDGE,"E139"),sQuery(id+"F4.wireOp",EDGE,"E140"),sQuery(id+"F4.wireOp",EDGE,"E141.trimOffspring"),sQuery(id+"F4.wireOp",EDGE,"E142"),sQuery(id+"F4.wireOp",EDGE,"E143"),sQuery(id+"F4.wireOp",EDGE,"E145"),sQuery(id+"F4.wireOp",EDGE,"E146"),sQuery(id+"F4.wireOp",EDGE,"E147"),sQuery(id+"F4.wireOp",EDGE,"E149.trimOffspring"),sQuery(id+"F4.wireOp",EDGE,"E150"),sQuery(id+"F4.wireOp",EDGE,"E174"),sQuery(id+"F4.wireOp",EDGE,"E151"),sQuery(id+"F4.wireOp",EDGE,"E152"),sQuery(id+"F4.wireOp",EDGE,"E153.trimOffspring"),sQuery(id+"F4.wireOp",EDGE,"E154"),sQuery(id+"F4.wireOp",EDGE,"E155"),sQuery(id+"F4.wireOp",EDGE,"I5dM6OyK-C2i5-N1ZM-TPve-bCS8jZquYYvb"),sQuery(id+"F4.wireOp",EDGE,"E156"),sQuery(id+"F4.wireOp",EDGE,"E157"),sQuery(id+"F4.wireOp",EDGE,"EQ092Qmf-d7RL-dsFj-pDk6-DLwWH4ga1MS3"),sQuery(id+"F4.wireOp",EDGE,"v4hw12ON-Kn0A-zcPN-AWdy-wjujSs07YwIl"),sQuery(id+"F4.wireOp",EDGE,"E169"),sQuery(id+"F4.wireOp",EDGE,"E170"),sQuery(id+"F4.wireOp",EDGE,"zHJcAi4G-vBjZ-PVc6-LSNt-6IGNiOixcgHz"),sQuery(id+"F4.wireOp",EDGE,"2icb326b-f8xt-jkox-nxTX-71DODKz5sswn"),sQuery(id+"F4.wireOp",EDGE,"DX3dQZYj-01vy-VJUN-FvUS-dIxg25u6yKv1"),sQuery(id+"F4.wireOp",EDGE,"vxZwufvW-1V3q-RiER-lRlK-IPzvBX9lEgKX"),sQuery(id+"F4.wireOp",EDGE,"E158"),sQuery(id+"F4.wireOp",EDGE,"E159"),sQuery(id+"F4.wireOp",EDGE,"Qwjh03jz-hG1A-jDlJ-MnOI-GFsmHNh0qciF"),sQuery(id+"F4.wireOp",EDGE,"E171"),sQuery(id+"F4.wireOp",EDGE,"E175"),sQuery(id+"F4.wireOp",EDGE,"TUlHPbTQ-i3I6-dmwq-wYJE-hk0mlEAQnZBi"),sQuery(id+"F4.wireOp",EDGE,"E172"),sQuery(id+"F4.wireOp",EDGE,"E173"),sQuery(id+"F4.wireOp",EDGE,"tHNRsyOz-VRlC-hlZC-n81j-1N2cYH4iIsKC"),sQuery(id+"F4.wireOp",EDGE,"E176"),sQuery(id+"F4.wireOp",EDGE,"46cc8c59-18d4-4094-b739-0333371662790.MirrorCS"),sQuery(id+"F4.wireOp",EDGE,"E124"),sQuery(id+"F4.wireOp",EDGE,"46cc8c59-18d4-4094-b739-0333371662792.MirrorCS"),sQuery(id+"F4.wireOp",EDGE,"46cc8c59-18d4-4094-b739-0333371662793.MirrorCS"),sQuery(id+"F4.wireOp",EDGE,"46cc8c59-18d4-4094-b739-0333371662794.MirrorCS"),sQuery(id+"F4.wireOp",EDGE,"46cc8c59-18d4-4094-b739-0333371662795.MirrorCS"),sQuery(id+"F4.wireOp",EDGE,"46cc8c59-18d4-4094-b739-0333371662796.MirrorCS"),sQuery(id+"F4.wireOp",EDGE,"46cc8c59-18d4-4094-b739-0333371662797.MirrorCS"),sQuery(id+"F4.wireOp",EDGE,"46cc8c59-18d4-4094-b739-0333371662798.MirrorCS"),sQuery(id+"F4.wireOp",EDGE,"46cc8c59-18d4-4094-b739-0333371662799.MirrorCS"),sQuery(id+"F4.wireOp",EDGE,"46cc8c59-18d4-4094-b739-03333716627910.MirrorCS"),sQuery(id+"F4.wireOp",EDGE,"46cc8c59-18d4-4094-b739-03333716627911.MirrorCS"),sQuery(id+"F4.wireOp",EDGE,"46cc8c59-18d4-4094-b739-03333716627912.MirrorCS"),sQuery(id+"F4.wireOp",EDGE,"46cc8c59-18d4-4094-b739-03333716627913.MirrorCS"),sQuery(id+"F4.wireOp",EDGE,"46cc8c59-18d4-4094-b739-03333716627914.MirrorCS"),sQuery(id+"F4.wireOp",EDGE,"46cc8c59-18d4-4094-b739-03333716627915.MirrorCS"),sQuery(id+"F4.wireOp",EDGE,"46cc8c59-18d4-4094-b739-03333716627916.MirrorCS"),sQuery(id+"F4.wireOp",EDGE,"46cc8c59-18d4-4094-b739-03333716627917.MirrorCS"),sQuery(id+"F4.wireOp",EDGE,"46cc8c59-18d4-4094-b739-03333716627918.MirrorCS"),sQuery(id+"F4.wireOp",EDGE,"46cc8c59-18d4-4094-b739-03333716627919.MirrorCS"),sQuery(id+"F4.wireOp",EDGE,"46cc8c59-18d4-4094-b739-03333716627920.MirrorCS"),sQuery(id+"F4.wireOp",EDGE,"46cc8c59-18d4-4094-b739-03333716627921.MirrorCS"),sQuery(id+"F4.wireOp",EDGE,"46cc8c59-18d4-4094-b739-03333716627922.MirrorCS"),sQuery(id+"F4.wireOp",EDGE,"46cc8c59-18d4-4094-b739-03333716627923.MirrorCS"),sQuery(id+"F4.wireOp",EDGE,"46cc8c59-18d4-4094-b739-03333716627924.MirrorCS"),sQuery(id+"F4.wireOp",EDGE,"46cc8c59-18d4-4094-b739-03333716627925.MirrorCS"),sQuery(id+"F4.wireOp",EDGE,"46cc8c59-18d4-4094-b739-03333716627926.MirrorCS"),sQuery(id+"F4.wireOp",EDGE,"46cc8c59-18d4-4094-b739-03333716627927.MirrorCS"),sQuery(id+"F4.wireOp",EDGE,"46cc8c59-18d4-4094-b739-03333716627928.MirrorCS"),sQuery(id+"F4.wireOp",EDGE,"46cc8c59-18d4-4094-b739-03333716627929.MirrorCS"),sQuery(id+"F4.wireOp",EDGE,"46cc8c59-18d4-4094-b739-03333716627930.MirrorCS"),sQuery(id+"F4.wireOp",EDGE,"46cc8c59-18d4-4094-b739-03333716627931.MirrorCS"),sQuery(id+"F4.wireOp",EDGE,"46cc8c59-18d4-4094-b739-03333716627932.MirrorCS"),sQuery(id+"F4.wireOp",EDGE,"46cc8c59-18d4-4094-b739-03333716627933.MirrorCS"),sQuery(id+"F4.wireOp",EDGE,"46cc8c59-18d4-4094-b739-03333716627937.MirrorC"),sQuery(id+"F4.wireOp",EDGE,"E164.MirrorCS"),sQuery(id+"F4.wireOp",EDGE,"E162.MirrorCS"),sQuery(id+"F4.wireOp",EDGE,"E163.MirrorCS"),sQuery(id+"F4.wireOp",EDGE,"VkYVsUMz-jEfg-iXTA-U9YV-3PSOp7gkSMdf"),sQuery(id+"F4.wireOp",EDGE,"E177")])]});
            transform(context, id + "F7", {"entities" : qUnion([Q0]), "transformType" : TransformType.TRANSLATION_3D, "dx" : 0 * mm, "dy" : 0 * mm, "dz" : 9.14 * mm, "makeCopy" : false});
        }
        {
            var Q0;
            Q0=makeQuery(id+"F3.opExtrude","SWEPT_EDGE",EDGE,{"disambiguationData":[OSD([sQuery(id+"F2.wireOp",EDGE,"E115"),sQuery(id+"F2.wireOp",EDGE,"E120.trimOffspring"),sQuery(id+"F2.wireOp",EDGE,"E121")])]});
            fillet(context, id + "F8", {"entities" : qUnion([Q0]), "radius" : 5.08 * mm, "tangentPropagation" : true, "allowEdgeOverflow" : false});
        }
    });
